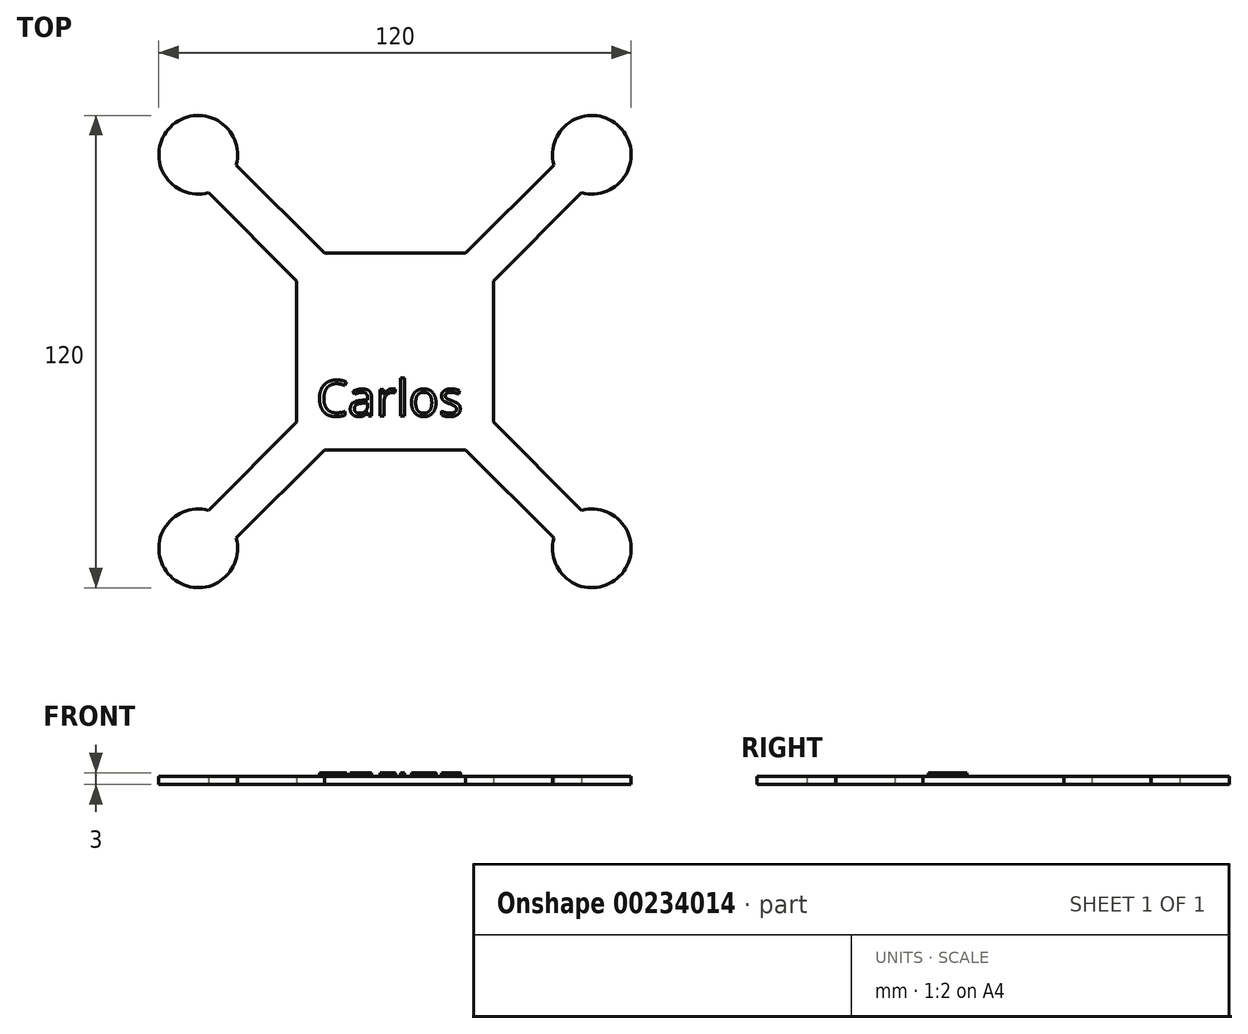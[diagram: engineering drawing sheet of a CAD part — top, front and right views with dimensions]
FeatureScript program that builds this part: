
annotation { "Feature Type Name" : "Feature", "Feature Type Description" : "" }
export const myFeature = defineFeature(function(context is Context, id is Id, definition is map)
    precondition{}
    {
        {
            var Q0;
            Q0=qCreatedBy(makeId("Top.planeOp"),FACE);
            var sketch = newSketch(context, id + "F0", { "sketchPlane" : qUnion([Q0])});
            skPoint(sketch, "E0.middle", {"position": v(0, 0) * mm});
            skLineSegment(sketch, "E1.bottom", {"start": v(-17.93, -25) * mm, "end": v(17.93, -25) * mm});
            skLineSegment(sketch, "E1.top", {"start": v(-17.93, 25) * mm, "end": v(17.93, 25) * mm});
            skLineSegment(sketch, "E1.left", {"start": v(-25, -17.93) * mm, "end": v(-25, 17.93) * mm});
            skLineSegment(sketch, "E1.right", {"start": v(25, -17.93) * mm, "end": v(25, 17.93) * mm});
            skArc(sketch, "E2", {"start": v(-40.34, 47.41) * mm, "mid": v(-57.07, 57.07) * mm, "end": v(-47.41, 40.34) * mm});
            skArc(sketch, "E3", {"start": v(47.41, 40.34) * mm, "mid": v(57.07, 57.07) * mm, "end": v(40.34, 47.41) * mm});
            skArc(sketch, "E4", {"start": v(-47.41, -40.34) * mm, "mid": v(-57.07, -57.07) * mm, "end": v(-40.34, -47.41) * mm});
            skArc(sketch, "E5", {"start": v(40.34, -47.41) * mm, "mid": v(57.07, -57.07) * mm, "end": v(47.41, -40.34) * mm});
            skLineSegment(sketch, "E6.0", {"start": v(25, 17.93) * mm, "end": v(47.41, 40.34) * mm});
            skLineSegment(sketch, "E7.0", {"start": v(-17.93, -25) * mm, "end": v(-40.34, -47.41) * mm});
            skLineSegment(sketch, "E8.0", {"start": v(17.93, -25) * mm, "end": v(40.34, -47.41) * mm});
            skLineSegment(sketch, "E9.0", {"start": v(17.93, 25) * mm, "end": v(40.34, 47.41) * mm});
            skLineSegment(sketch, "E10.0", {"start": v(-40.34, 47.41) * mm, "end": v(-17.93, 25) * mm});
            skLineSegment(sketch, "E11.0", {"start": v(25, -17.93) * mm, "end": v(47.41, -40.34) * mm});
            skLineSegment(sketch, "E12.0", {"start": v(-25, -17.93) * mm, "end": v(-47.41, -40.34) * mm});
            skLineSegment(sketch, "E13.trimOffspring", {"start": v(-47.41, 40.34) * mm, "end": v(-25, 17.93) * mm});
            skPoint(sketch, "E14.orphan", {"position": v(-25, -25) * mm});
            skPoint(sketch, "E15.orphan", {"position": v(25, -25) * mm});
            skPoint(sketch, "E16.orphan", {"position": v(25, 25) * mm});
            skPoint(sketch, "E17.orphan", {"position": v(-25, 25) * mm});
            skSolve(sketch);
        }
        {
            var Q0;
            Q0=makeQuery(id+"F0.imprint","IMPRINT",FACE,{"disambiguationData":[TD([[makeQuery(id+"F0.imprint","IMPRINT",EDGE,{"derivedFrom":sQuery(id+"F0.wireOp",EDGE,"E1.bottom")}),1.0]])]});
            extrude(context, id + "F1", {"entities" : qUnion([Q0]), "depth" : 2 * mm});
        }
        {
            var Q0;
            Q0=makeQuery(id+"F1.opExtrude","CAP_FACE",FACE,{"disambiguationData":[OSD([sQuery(id+"F0.wireOp",EDGE,"E1.bottom"),sQuery(id+"F0.wireOp",EDGE,"E1.top"),sQuery(id+"F0.wireOp",EDGE,"E1.left"),sQuery(id+"F0.wireOp",EDGE,"E1.right"),sQuery(id+"F0.wireOp",EDGE,"E2"),sQuery(id+"F0.wireOp",EDGE,"E3"),sQuery(id+"F0.wireOp",EDGE,"E4"),sQuery(id+"F0.wireOp",EDGE,"E5"),sQuery(id+"F0.wireOp",EDGE,"E6.0"),sQuery(id+"F0.wireOp",EDGE,"E7.0"),sQuery(id+"F0.wireOp",EDGE,"E8.0"),sQuery(id+"F0.wireOp",EDGE,"E9.0"),sQuery(id+"F0.wireOp",EDGE,"E10.0"),sQuery(id+"F0.wireOp",EDGE,"E11.0"),sQuery(id+"F0.wireOp",EDGE,"E12.0"),sQuery(id+"F0.wireOp",EDGE,"E13.trimOffspring")])],"isStart":false});
            var sketch = newSketch(context, id + "F2", { "sketchPlane" : qUnion([Q0])});
            skText(sketch, "E18", { "text": "Carlos", "fontName": "OpenSans-Regular.ttf"});
            const initialGuessF2  = {"E18": [-0.01997, -0.0164, 1, 0, 0.00913]};
            skSetInitialGuess(sketch, initialGuessF2);
            skSolve(sketch);
        }
        {
            var Q0;
            Q0 = qSketchRegion(id + "F2", true);
            extrude(context, id + "F3", {"entities" : qUnion([Q0]), "operationType" : NewBodyOperationType.ADD, "depth" : 1 * mm});
        }
    });
